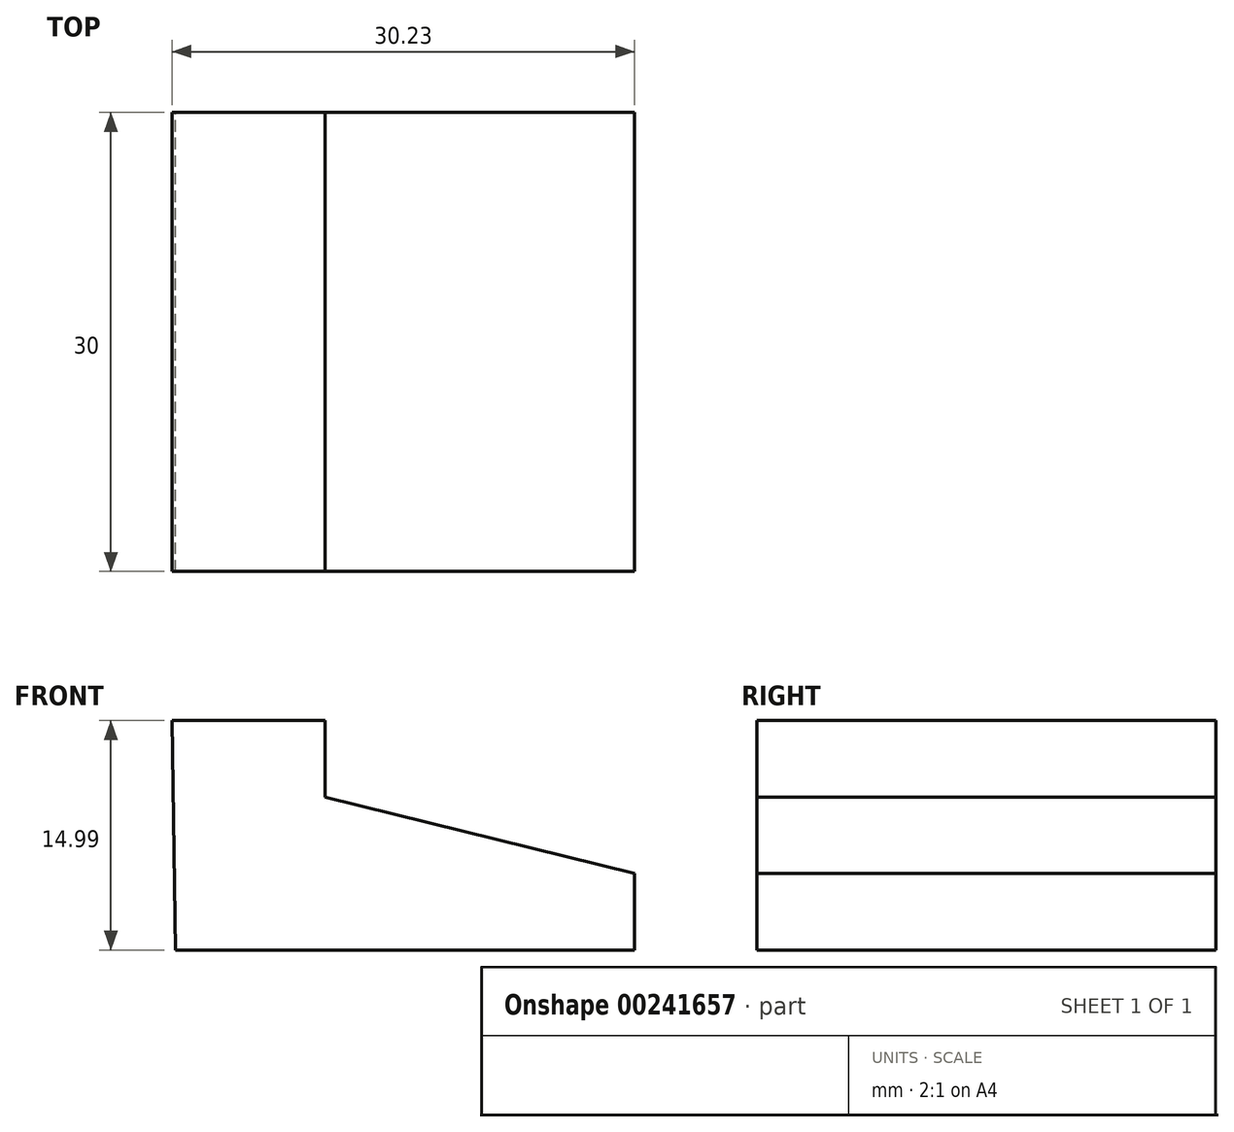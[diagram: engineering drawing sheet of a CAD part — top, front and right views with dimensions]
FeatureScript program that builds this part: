
annotation { "Feature Type Name" : "Feature", "Feature Type Description" : "" }
export const myFeature = defineFeature(function(context is Context, id is Id, definition is map)
    precondition{}
    {
        {
            var Q0;
            Q0=qCreatedBy(makeId("Front.planeOp"),FACE);
            var sketch = newSketch(context, id + "F0", { "sketchPlane" : qUnion([Q0])});
            skLineSegment(sketch, "E0", {"start": v(-8.1, 5.36) * mm, "end": v(21.9, 5.36) * mm});
            skLineSegment(sketch, "E1", {"start": v(21.9, 5.36) * mm, "end": v(21.9, 10.36) * mm});
            skLineSegment(sketch, "E2", {"start": v(21.9, 10.36) * mm, "end": v(1.67, 15.35) * mm});
            skLineSegment(sketch, "E3", {"start": v(1.67, 15.35) * mm, "end": v(1.67, 20.35) * mm});
            skLineSegment(sketch, "E4", {"start": v(1.67, 20.35) * mm, "end": v(-8.33, 20.35) * mm});
            skLineSegment(sketch, "E5", {"start": v(-8.1, 5.36) * mm, "end": v(-8.33, 20.35) * mm});
            skSolve(sketch);
        }
        {
            var Q0;
            Q0=makeQuery(id+"F0.imprint","IMPRINT",FACE,{"disambiguationData":[TD([[makeQuery(id+"F0.imprint","IMPRINT",EDGE,{"derivedFrom":sQuery(id+"F0.wireOp",EDGE,"E0")}),1.0]])]});
            extrude(context, id + "F1", {"entities" : qUnion([Q0]), "depth" : 30 * mm});
        }
    });
